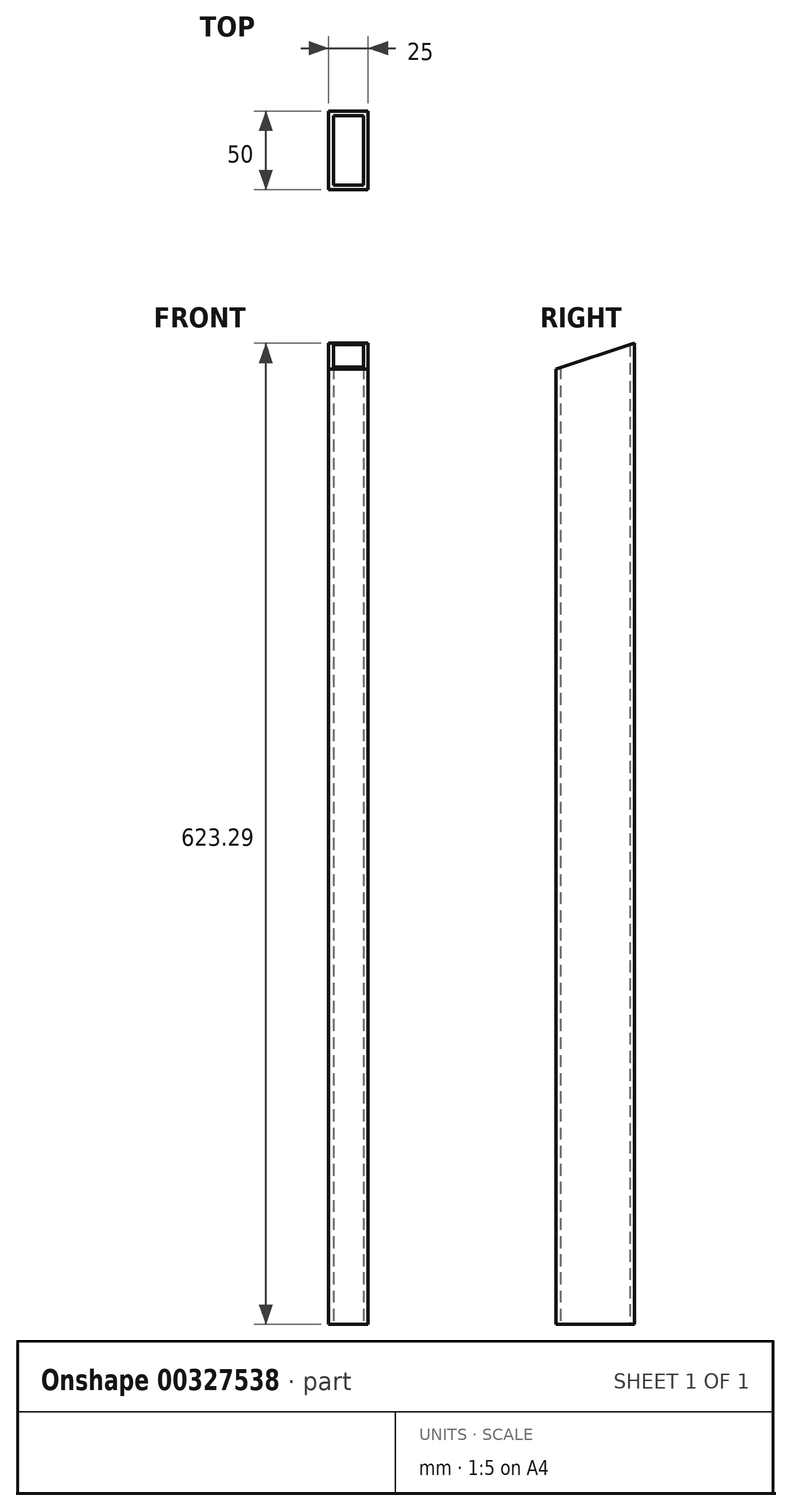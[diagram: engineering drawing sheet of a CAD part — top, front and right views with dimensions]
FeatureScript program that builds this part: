
annotation { "Feature Type Name" : "Feature", "Feature Type Description" : "" }
export const myFeature = defineFeature(function(context is Context, id is Id, definition is map)
    precondition{}
    {
        {
            var Q0;
            Q0=qCreatedBy(makeId("Right.planeOp"),FACE);
            var sketch = newSketch(context, id + "F0", { "sketchPlane" : qUnion([Q0])});
            skLineSegment(sketch, "E0", {"start": v(0, 0) * mm, "end": v(2288, 0) * mm});
            skLineSegment(sketch, "E1", {"start": v(2288, 0) * mm, "end": v(2288, 684.37) * mm});
            skLineSegment(sketch, "E2", {"start": v(2100, 0) * mm, "end": v(2100, 623.29) * mm});
            skLineSegment(sketch, "E3", {"start": v(2050, 0) * mm, "end": v(2050, 607.04) * mm});
            skLineSegment(sketch, "E4", {"start": v(1862, 545.95) * mm, "end": v(2288, 684.37) * mm});
            skLineSegment(sketch, "E5", {"start": v(2288, 684.37) * mm, "end": v(2279.35, 711) * mm});
            skLineSegment(sketch, "E6", {"start": v(2100, 623.29) * mm, "end": v(2091.35, 649.92) * mm});
            skLineSegment(sketch, "E7", {"start": v(2050, 607.04) * mm, "end": v(2041.35, 633.67) * mm});
            skLineSegment(sketch, "E8", {"start": v(2279.35, 711) * mm, "end": v(2091.35, 649.92) * mm});
            skLineSegment(sketch, "E9", {"start": v(2091.35, 649.92) * mm, "end": v(2041.35, 633.67) * mm});
            skLineSegment(sketch, "E10", {"start": v(2041.35, 633.67) * mm, "end": v(1853.35, 572.58) * mm});
            skLineSegment(sketch, "E11", {"start": v(1853.35, 572.58) * mm, "end": v(1862, 545.95) * mm});
            skLineSegment(sketch, "E12", {"start": v(1854.27, 569.73) * mm, "end": v(2280.27, 708.15) * mm});
            skSolve(sketch);
        }
        {
            var Q0;
            {var subQ0=sQuery(id+"F0.wireOp",EDGE,"E2");Q0=makeQuery(id+"F0.imprint","IMPRINT",FACE,{"disambiguationData":[TD([[makeQuery(id+"F0.imprint","IMPRINT",EDGE,{"derivedFrom":subQ0}),1.0]])]});}
            extrude(context, id + "F1", {"entities" : qUnion([Q0]), "depth" : 25 * mm});
        }
        {
            var Q0;
            Q0=makeQuery(id+"F1.opExtrude","SWEPT_FACE",FACE,{"disambiguationData":[OSD([sQuery(id+"F0.wireOp",EDGE,"E0")])]});
            var sketch = newSketch(context, id + "F2", { "sketchPlane" : qUnion([Q0])});
            skLineSegment(sketch, "E13", {"start": v(25, -2100) * mm, "end": v(0, -2050) * mm});
            skLineSegment(sketch, "E14", {"start": v(0, -2050) * mm, "end": v(0, -2100) * mm});
            skLineSegment(sketch, "E15", {"start": v(0, -2100) * mm, "end": v(25, -2050) * mm});
            skPoint(sketch, "E16.middle", {"position": v(12.5, -2075) * mm});
            skLineSegment(sketch, "E17.bottom", {"start": v(22, -2097) * mm, "end": v(3, -2097) * mm});
            skLineSegment(sketch, "E17.top", {"start": v(22, -2053) * mm, "end": v(3, -2053) * mm});
            skLineSegment(sketch, "E17.left", {"start": v(22, -2097) * mm, "end": v(22, -2053) * mm});
            skLineSegment(sketch, "E17.right", {"start": v(3, -2097) * mm, "end": v(3, -2053) * mm});
            skSolve(sketch);
        }
        {
            var Q0;
            {var subQ0=sQuery(id+"F2.wireOp",EDGE,"E17.left");var subQ1=sQuery(id+"F2.wireOp",EDGE,"E13");var subQ2=makeQuery(id+"F2.imprint","INTERSECT",VERTEX,{"derivedFrom":[subQ1,subQ0]});Q0=makeQuery(id+"F2.imprint","IMPRINT",FACE,{"disambiguationData":[TD([[makeQuery(id+"F2.imprint","IMPRINT",EDGE,{"disambiguationData":[TD([[subQ2,-1.0]])],"derivedFrom":subQ1}),-1.0]])]});}
            var Q1;
            {var subQ0=sQuery(id+"F2.wireOp",EDGE,"E17.bottom");Q1=makeQuery(id+"F2.imprint","IMPRINT",FACE,{"disambiguationData":[TD([[makeQuery(id+"F2.imprint","IMPRINT",EDGE,{"derivedFrom":subQ0}),-1.0]])]});}
            var Q2;
            {var subQ0=sQuery(id+"F2.wireOp",EDGE,"E15");var subQ1=sQuery(id+"F2.wireOp",EDGE,"E13");var subQ2=makeQuery(id+"F2.imprint","INTERSECT",VERTEX,{"derivedFrom":[subQ1,subQ0]});Q2=makeQuery(id+"F2.imprint","IMPRINT",FACE,{"disambiguationData":[TD([[makeQuery(id+"F2.imprint","IMPRINT",EDGE,{"disambiguationData":[TD([[subQ2,-1.0]])],"derivedFrom":subQ1}),1.0]])]});}
            var Q3;
            {var subQ1=sQuery(id+"F2.wireOp",EDGE,"E17.top");Q3=makeQuery(id+"F2.imprint","IMPRINT",FACE,{"disambiguationData":[TD([[makeQuery(id+"F2.imprint","IMPRINT",EDGE,{"derivedFrom":subQ1}),1.0]])]});}
            extrude(context, id + "F3", {"entities" : qUnion([Q0, Q1, Q2, Q3]), "operationType" : NewBodyOperationType.REMOVE, "oppositeDirection" : true, "depth" : 1000 * mm});
        }
    });
